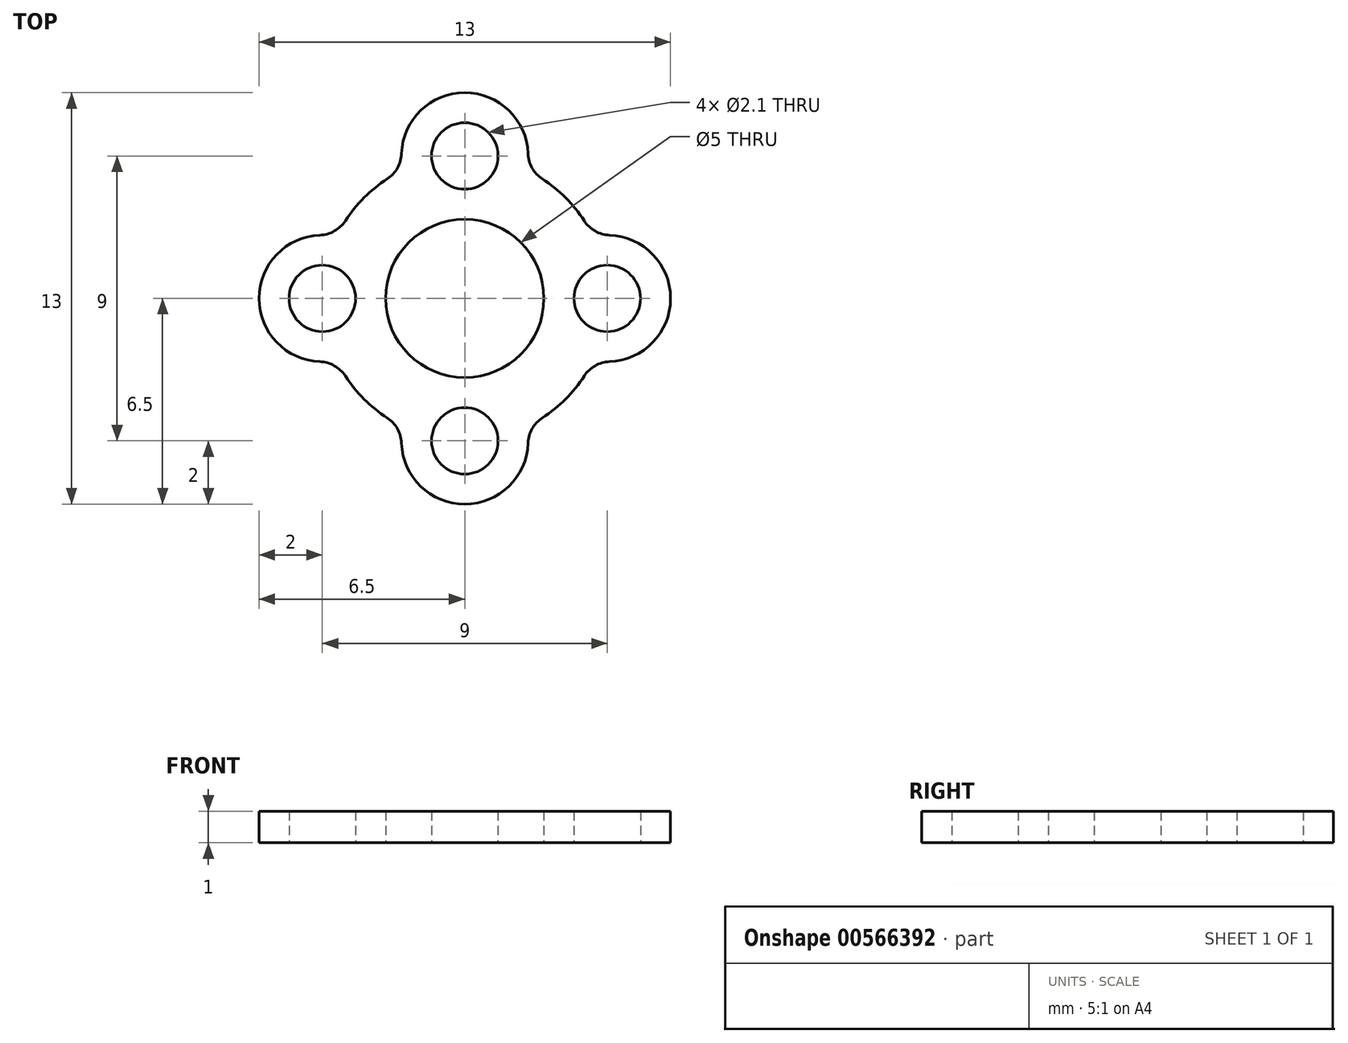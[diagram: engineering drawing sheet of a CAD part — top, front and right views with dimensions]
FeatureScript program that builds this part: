
annotation { "Feature Type Name" : "Feature", "Feature Type Description" : "" }
export const myFeature = defineFeature(function(context is Context, id is Id, definition is map)
    precondition{}
    {
        {
            var Q0;
            Q0=qCreatedBy(makeId("Top.planeOp"),FACE);
            var sketch = newSketch(context, id + "F0", { "sketchPlane" : qUnion([Q0])});
            skCircle(sketch, "E0", {"center": v(0, 0) * mm, "radius": 2.5 * mm});
            skCircle(sketch, "E1", {"center": v(0, 0) * mm, "radius": 4.5 * mm});
            skLineSegment(sketch, "E2", {"start": v(0, 9.73) * mm, "end": v(0, -9.1) * mm});
            skLineSegment(sketch, "E3", {"start": v(-12.9, 0) * mm, "end": v(17.78, 0) * mm});
            skCircle(sketch, "E4", {"center": v(0, 4.5) * mm, "radius": 1.05 * mm});
            skCircle(sketch, "E5", {"center": v(4.5, 0) * mm, "radius": 1.05 * mm});
            skCircle(sketch, "E6.MirrorC", {"center": v(0, -4.5) * mm, "radius": 1.05 * mm});
            skCircle(sketch, "E7.MirrorC", {"center": v(-4.5, 0) * mm, "radius": 1.05 * mm});
            skCircle(sketch, "E8", {"center": v(0, 0) * mm, "radius": 6.5 * mm});
            skCircle(sketch, "E9", {"center": v(0, 4.5) * mm, "radius": 2 * mm});
            skCircle(sketch, "E10", {"center": v(4.5, 0) * mm, "radius": 2 * mm});
            skCircle(sketch, "E11.MirrorC", {"center": v(0, -4.5) * mm, "radius": 2 * mm});
            skCircle(sketch, "E12.MirrorC", {"center": v(-4.5, 0) * mm, "radius": 2 * mm});
            skSolve(sketch);
        }
        {
            var Q0;
            {var subQ0=sQuery(id+"F0.wireOp",EDGE,"E9");var subQ5=sQuery(id+"F0.wireOp",EDGE,"E1");var subQ6=makeQuery(id+"F0.imprint","INTERSECT",VERTEX,{"disambiguationData":[OD(1.0)],"derivedFrom":[subQ5,subQ0]});Q0=makeQuery(id+"F0.imprint","IMPRINT",FACE,{"disambiguationData":[TD([[makeQuery(id+"F0.imprint","IMPRINT",EDGE,{"disambiguationData":[TD([[subQ6,-1.0]])],"derivedFrom":subQ5}),1.0]])]});}
            var Q1;
            {var subQ0=sQuery(id+"F0.wireOp",EDGE,"E12.MirrorC");var subQ1=sQuery(id+"F0.wireOp",EDGE,"E1");var subQ2=makeQuery(id+"F0.imprint","INTERSECT",VERTEX,{"disambiguationData":[OD(0.0)],"derivedFrom":[subQ1,subQ0]});Q1=makeQuery(id+"F0.imprint","IMPRINT",FACE,{"disambiguationData":[TD([[makeQuery(id+"F0.imprint","IMPRINT",EDGE,{"disambiguationData":[TD([[subQ2,-1.0]])],"derivedFrom":subQ1}),1.0]])]});}
            var Q2;
            {var subQ0=sQuery(id+"F0.wireOp",EDGE,"E7.MirrorC");var subQ1=sQuery(id+"F0.wireOp",EDGE,"E1");var subQ2=makeQuery(id+"F0.imprint","INTERSECT",VERTEX,{"disambiguationData":[OD(1.0)],"derivedFrom":[subQ1,subQ0]});Q2=makeQuery(id+"F0.imprint","IMPRINT",FACE,{"disambiguationData":[TD([[makeQuery(id+"F0.imprint","IMPRINT",EDGE,{"disambiguationData":[TD([[subQ2,-1.0]])],"derivedFrom":subQ1}),1.0]])]});}
            var Q3;
            {var subQ0=sQuery(id+"F0.wireOp",EDGE,"E12.MirrorC");var subQ5=sQuery(id+"F0.wireOp",EDGE,"E1");var subQ6=makeQuery(id+"F0.imprint","INTERSECT",VERTEX,{"disambiguationData":[OD(1.0)],"derivedFrom":[subQ5,subQ0]});Q3=makeQuery(id+"F0.imprint","IMPRINT",FACE,{"disambiguationData":[TD([[makeQuery(id+"F0.imprint","IMPRINT",EDGE,{"disambiguationData":[TD([[subQ6,-1.0]])],"derivedFrom":subQ5}),1.0]])]});}
            var Q4;
            {var subQ3=sQuery(id+"F0.wireOp",EDGE,"E11.MirrorC");var subQ5=sQuery(id+"F0.wireOp",EDGE,"E1");var subQ6=makeQuery(id+"F0.imprint","INTERSECT",VERTEX,{"disambiguationData":[OD(1.0)],"derivedFrom":[subQ5,subQ3]});Q4=makeQuery(id+"F0.imprint","IMPRINT",FACE,{"disambiguationData":[TD([[makeQuery(id+"F0.imprint","IMPRINT",EDGE,{"disambiguationData":[TD([[subQ6,-1.0]])],"derivedFrom":subQ5}),1.0]])]});}
            var Q5;
            {var subQ0=sQuery(id+"F0.wireOp",EDGE,"E10");var subQ1=sQuery(id+"F0.wireOp",EDGE,"E1");var subQ2=makeQuery(id+"F0.imprint","INTERSECT",VERTEX,{"disambiguationData":[OD(1.0)],"derivedFrom":[subQ1,subQ0]});Q5=makeQuery(id+"F0.imprint","IMPRINT",FACE,{"disambiguationData":[TD([[makeQuery(id+"F0.imprint","IMPRINT",EDGE,{"disambiguationData":[TD([[subQ2,-1.0]])],"derivedFrom":subQ1}),1.0]])]});}
            var Q6;
            {var subQ0=sQuery(id+"F0.wireOp",EDGE,"E5");var subQ1=sQuery(id+"F0.wireOp",EDGE,"E1");var subQ2=makeQuery(id+"F0.imprint","INTERSECT",VERTEX,{"disambiguationData":[OD(0.0)],"derivedFrom":[subQ1,subQ0]});Q6=makeQuery(id+"F0.imprint","IMPRINT",FACE,{"disambiguationData":[TD([[makeQuery(id+"F0.imprint","IMPRINT",EDGE,{"disambiguationData":[TD([[subQ2,-1.0]])],"derivedFrom":subQ1}),1.0]])]});}
            var Q7;
            {var subQ3=sQuery(id+"F0.wireOp",EDGE,"E10");var subQ5=sQuery(id+"F0.wireOp",EDGE,"E1");var subQ6=makeQuery(id+"F0.imprint","INTERSECT",VERTEX,{"disambiguationData":[OD(0.0)],"derivedFrom":[subQ5,subQ3]});Q7=makeQuery(id+"F0.imprint","IMPRINT",FACE,{"disambiguationData":[TD([[makeQuery(id+"F0.imprint","IMPRINT",EDGE,{"disambiguationData":[TD([[subQ6,-1.0]])],"derivedFrom":subQ5}),1.0]])]});}
            var Q8;
            {var subQ0=sQuery(id+"F0.wireOp",EDGE,"E9");var subQ1=sQuery(id+"F0.wireOp",EDGE,"E1");var subQ2=makeQuery(id+"F0.imprint","INTERSECT",VERTEX,{"disambiguationData":[OD(0.0)],"derivedFrom":[subQ1,subQ0]});Q8=makeQuery(id+"F0.imprint","IMPRINT",FACE,{"disambiguationData":[TD([[makeQuery(id+"F0.imprint","IMPRINT",EDGE,{"disambiguationData":[TD([[subQ2,-1.0]])],"derivedFrom":subQ1}),1.0]])]});}
            var Q9;
            {var subQ0=sQuery(id+"F0.wireOp",EDGE,"E4");var subQ1=sQuery(id+"F0.wireOp",EDGE,"E1");var subQ2=makeQuery(id+"F0.imprint","INTERSECT",VERTEX,{"disambiguationData":[OD(1.0)],"derivedFrom":[subQ1,subQ0]});Q9=makeQuery(id+"F0.imprint","IMPRINT",FACE,{"disambiguationData":[TD([[makeQuery(id+"F0.imprint","IMPRINT",EDGE,{"disambiguationData":[TD([[subQ2,-1.0]])],"derivedFrom":subQ1}),1.0]])]});}
            var Q10;
            {var subQ0=sQuery(id+"F0.wireOp",EDGE,"E4");var subQ1=sQuery(id+"F0.wireOp",EDGE,"E1");var subQ2=makeQuery(id+"F0.imprint","INTERSECT",VERTEX,{"disambiguationData":[OD(1.0)],"derivedFrom":[subQ1,subQ0]});Q10=makeQuery(id+"F0.imprint","IMPRINT",FACE,{"disambiguationData":[TD([[makeQuery(id+"F0.imprint","IMPRINT",EDGE,{"disambiguationData":[TD([[subQ2,-1.0]])],"derivedFrom":subQ1}),-1.0]])]});}
            var Q11;
            {var subQ0=sQuery(id+"F0.wireOp",EDGE,"E9");var subQ1=sQuery(id+"F0.wireOp",EDGE,"E1");var subQ2=makeQuery(id+"F0.imprint","INTERSECT",VERTEX,{"disambiguationData":[OD(0.0)],"derivedFrom":[subQ1,subQ0]});Q11=makeQuery(id+"F0.imprint","IMPRINT",FACE,{"disambiguationData":[TD([[makeQuery(id+"F0.imprint","IMPRINT",EDGE,{"disambiguationData":[TD([[subQ2,-1.0]])],"derivedFrom":subQ1}),-1.0]])]});}
            var Q12;
            {var subQ0=sQuery(id+"F0.wireOp",EDGE,"E5");var subQ1=sQuery(id+"F0.wireOp",EDGE,"E1");var subQ2=makeQuery(id+"F0.imprint","INTERSECT",VERTEX,{"disambiguationData":[OD(0.0)],"derivedFrom":[subQ1,subQ0]});Q12=makeQuery(id+"F0.imprint","IMPRINT",FACE,{"disambiguationData":[TD([[makeQuery(id+"F0.imprint","IMPRINT",EDGE,{"disambiguationData":[TD([[subQ2,-1.0]])],"derivedFrom":subQ1}),-1.0]])]});}
            var Q13;
            {var subQ0=sQuery(id+"F0.wireOp",EDGE,"E10");var subQ1=sQuery(id+"F0.wireOp",EDGE,"E1");var subQ2=makeQuery(id+"F0.imprint","INTERSECT",VERTEX,{"disambiguationData":[OD(1.0)],"derivedFrom":[subQ1,subQ0]});Q13=makeQuery(id+"F0.imprint","IMPRINT",FACE,{"disambiguationData":[TD([[makeQuery(id+"F0.imprint","IMPRINT",EDGE,{"disambiguationData":[TD([[subQ2,-1.0]])],"derivedFrom":subQ1}),-1.0]])]});}
            var Q14;
            {var subQ0=sQuery(id+"F0.wireOp",EDGE,"E6.MirrorC");var subQ1=sQuery(id+"F0.wireOp",EDGE,"E1");var subQ2=makeQuery(id+"F0.imprint","INTERSECT",VERTEX,{"disambiguationData":[OD(1.0)],"derivedFrom":[subQ1,subQ0]});Q14=makeQuery(id+"F0.imprint","IMPRINT",FACE,{"disambiguationData":[TD([[makeQuery(id+"F0.imprint","IMPRINT",EDGE,{"disambiguationData":[TD([[subQ2,-1.0]])],"derivedFrom":subQ1}),1.0]])]});}
            var Q15;
            {var subQ0=sQuery(id+"F0.wireOp",EDGE,"E11.MirrorC");var subQ1=sQuery(id+"F0.wireOp",EDGE,"E1");var subQ2=makeQuery(id+"F0.imprint","INTERSECT",VERTEX,{"disambiguationData":[OD(0.0)],"derivedFrom":[subQ1,subQ0]});Q15=makeQuery(id+"F0.imprint","IMPRINT",FACE,{"disambiguationData":[TD([[makeQuery(id+"F0.imprint","IMPRINT",EDGE,{"disambiguationData":[TD([[subQ2,-1.0]])],"derivedFrom":subQ1}),1.0]])]});}
            var Q16;
            {var subQ0=sQuery(id+"F0.wireOp",EDGE,"E11.MirrorC");var subQ1=sQuery(id+"F0.wireOp",EDGE,"E1");var subQ2=makeQuery(id+"F0.imprint","INTERSECT",VERTEX,{"disambiguationData":[OD(0.0)],"derivedFrom":[subQ1,subQ0]});Q16=makeQuery(id+"F0.imprint","IMPRINT",FACE,{"disambiguationData":[TD([[makeQuery(id+"F0.imprint","IMPRINT",EDGE,{"disambiguationData":[TD([[subQ2,-1.0]])],"derivedFrom":subQ1}),-1.0]])]});}
            var Q17;
            {var subQ0=sQuery(id+"F0.wireOp",EDGE,"E6.MirrorC");var subQ1=sQuery(id+"F0.wireOp",EDGE,"E1");var subQ2=makeQuery(id+"F0.imprint","INTERSECT",VERTEX,{"disambiguationData":[OD(1.0)],"derivedFrom":[subQ1,subQ0]});Q17=makeQuery(id+"F0.imprint","IMPRINT",FACE,{"disambiguationData":[TD([[makeQuery(id+"F0.imprint","IMPRINT",EDGE,{"disambiguationData":[TD([[subQ2,-1.0]])],"derivedFrom":subQ1}),-1.0]])]});}
            var Q18;
            {var subQ0=sQuery(id+"F0.wireOp",EDGE,"E7.MirrorC");var subQ1=sQuery(id+"F0.wireOp",EDGE,"E1");var subQ2=makeQuery(id+"F0.imprint","INTERSECT",VERTEX,{"disambiguationData":[OD(1.0)],"derivedFrom":[subQ1,subQ0]});Q18=makeQuery(id+"F0.imprint","IMPRINT",FACE,{"disambiguationData":[TD([[makeQuery(id+"F0.imprint","IMPRINT",EDGE,{"disambiguationData":[TD([[subQ2,-1.0]])],"derivedFrom":subQ1}),-1.0]])]});}
            var Q19;
            {var subQ0=sQuery(id+"F0.wireOp",EDGE,"E12.MirrorC");var subQ1=sQuery(id+"F0.wireOp",EDGE,"E1");var subQ2=makeQuery(id+"F0.imprint","INTERSECT",VERTEX,{"disambiguationData":[OD(0.0)],"derivedFrom":[subQ1,subQ0]});Q19=makeQuery(id+"F0.imprint","IMPRINT",FACE,{"disambiguationData":[TD([[makeQuery(id+"F0.imprint","IMPRINT",EDGE,{"disambiguationData":[TD([[subQ2,-1.0]])],"derivedFrom":subQ1}),-1.0]])]});}
            extrude(context, id + "F1", {"entities" : qUnion([Q0, Q1, Q2, Q3, Q4, Q5, Q6, Q7, Q8, Q9, Q10, Q11, Q12, Q13, Q14, Q15, Q16, Q17, Q18, Q19]), "depth" : 1 * mm, "offsetDistance" : 25 * mm});
        }
        {
            var Q0;
            {var subQ0=sQuery(id+"F0.wireOp",EDGE,"E12.MirrorC");var subQ1=sQuery(id+"F0.wireOp",EDGE,"E1");Q0=makeQuery(id+"F1.opExtrude","SWEPT_EDGE",EDGE,{"disambiguationData":[OSD([subQ1,subQ0]),TDD([makeQuery(id+"F0.imprint","INTERSECT",VERTEX,{"disambiguationData":[OD(0.0)],"derivedFrom":[subQ1,subQ0]})])]});}
            var Q1;
            {var subQ0=sQuery(id+"F0.wireOp",EDGE,"E9");var subQ1=sQuery(id+"F0.wireOp",EDGE,"E1");Q1=makeQuery(id+"F1.opExtrude","SWEPT_EDGE",EDGE,{"disambiguationData":[OSD([subQ1,subQ0]),TDD([makeQuery(id+"F0.imprint","INTERSECT",VERTEX,{"disambiguationData":[OD(1.0)],"derivedFrom":[subQ1,subQ0]})])]});}
            var Q2;
            {var subQ0=sQuery(id+"F0.wireOp",EDGE,"E9");var subQ1=sQuery(id+"F0.wireOp",EDGE,"E1");Q2=makeQuery(id+"F1.opExtrude","SWEPT_EDGE",EDGE,{"disambiguationData":[OSD([subQ1,subQ0]),TDD([makeQuery(id+"F0.imprint","INTERSECT",VERTEX,{"disambiguationData":[OD(0.0)],"derivedFrom":[subQ1,subQ0]})])]});}
            var Q3;
            {var subQ0=sQuery(id+"F0.wireOp",EDGE,"E10");var subQ1=sQuery(id+"F0.wireOp",EDGE,"E1");Q3=makeQuery(id+"F1.opExtrude","SWEPT_EDGE",EDGE,{"disambiguationData":[OSD([subQ1,subQ0]),TDD([makeQuery(id+"F0.imprint","INTERSECT",VERTEX,{"disambiguationData":[OD(0.0)],"derivedFrom":[subQ1,subQ0]})])]});}
            var Q4;
            {var subQ0=sQuery(id+"F0.wireOp",EDGE,"E10");var subQ1=sQuery(id+"F0.wireOp",EDGE,"E1");Q4=makeQuery(id+"F1.opExtrude","SWEPT_EDGE",EDGE,{"disambiguationData":[OSD([subQ1,subQ0]),TDD([makeQuery(id+"F0.imprint","INTERSECT",VERTEX,{"disambiguationData":[OD(1.0)],"derivedFrom":[subQ1,subQ0]})])]});}
            var Q5;
            {var subQ0=sQuery(id+"F0.wireOp",EDGE,"E11.MirrorC");var subQ1=sQuery(id+"F0.wireOp",EDGE,"E1");Q5=makeQuery(id+"F1.opExtrude","SWEPT_EDGE",EDGE,{"disambiguationData":[OSD([subQ1,subQ0]),TDD([makeQuery(id+"F0.imprint","INTERSECT",VERTEX,{"disambiguationData":[OD(1.0)],"derivedFrom":[subQ1,subQ0]})])]});}
            var Q6;
            {var subQ0=sQuery(id+"F0.wireOp",EDGE,"E11.MirrorC");var subQ1=sQuery(id+"F0.wireOp",EDGE,"E1");Q6=makeQuery(id+"F1.opExtrude","SWEPT_EDGE",EDGE,{"disambiguationData":[OSD([subQ1,subQ0]),TDD([makeQuery(id+"F0.imprint","INTERSECT",VERTEX,{"disambiguationData":[OD(0.0)],"derivedFrom":[subQ1,subQ0]})])]});}
            var Q7;
            {var subQ0=sQuery(id+"F0.wireOp",EDGE,"E12.MirrorC");var subQ1=sQuery(id+"F0.wireOp",EDGE,"E1");Q7=makeQuery(id+"F1.opExtrude","SWEPT_EDGE",EDGE,{"disambiguationData":[OSD([subQ1,subQ0]),TDD([makeQuery(id+"F0.imprint","INTERSECT",VERTEX,{"disambiguationData":[OD(1.0)],"derivedFrom":[subQ1,subQ0]})])]});}
            fillet(context, id + "F2", {"entities" : qUnion([Q0, Q1, Q2, Q3, Q4, Q5, Q6, Q7]), "radius" : 1 * mm, "tangentPropagation" : true, "allowEdgeOverflow" : false});
        }
    });
